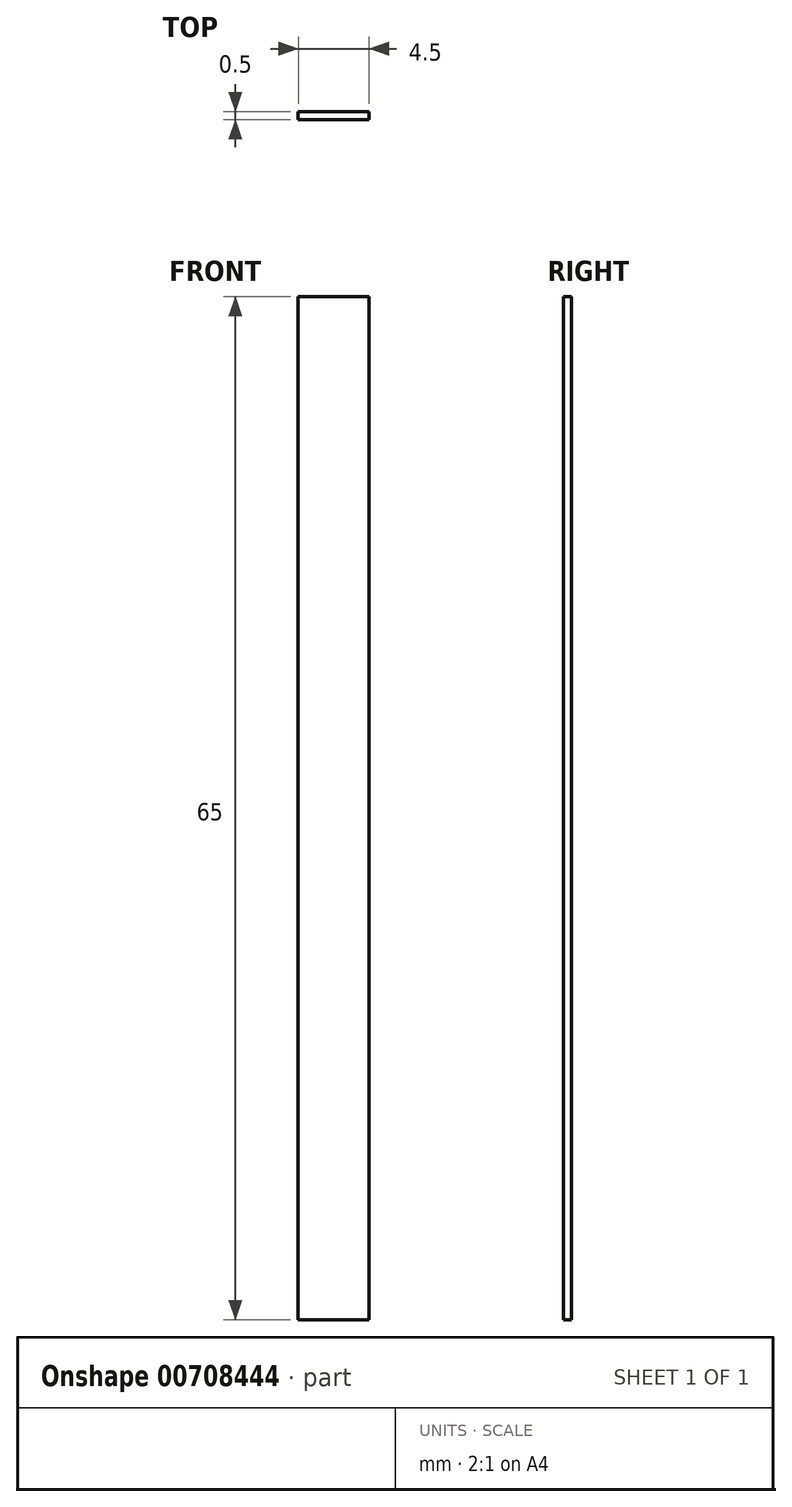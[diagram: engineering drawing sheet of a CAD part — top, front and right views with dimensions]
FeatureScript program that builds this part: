
annotation { "Feature Type Name" : "Feature", "Feature Type Description" : "" }
export const myFeature = defineFeature(function(context is Context, id is Id, definition is map)
    precondition{}
    {
        {
            var Q0;
            Q0=qCreatedBy(makeId("Front.planeOp"),FACE);
            var sketch = newSketch(context, id + "F0", { "sketchPlane" : qUnion([Q0])});
            skLineSegment(sketch, "E0.bottom", {"start": v(-2.36, 40.04) * mm, "end": v(2.14, 40.04) * mm});
            skLineSegment(sketch, "E0.top", {"start": v(-2.36, -24.96) * mm, "end": v(2.14, -24.96) * mm});
            skLineSegment(sketch, "E0.left", {"start": v(-2.36, 40.04) * mm, "end": v(-2.36, -24.96) * mm});
            skLineSegment(sketch, "E0.right", {"start": v(2.14, 40.04) * mm, "end": v(2.14, -24.96) * mm});
            skSolve(sketch);
        }
        {
            var Q0;
            Q0=qSketchRegion(id+"F0",true);
            extrude(context, id + "F1", {"entities" : qUnion([Q0]), "depth" : 0.5 * mm, "offsetDistance" : 25 * mm});
        }
    });
